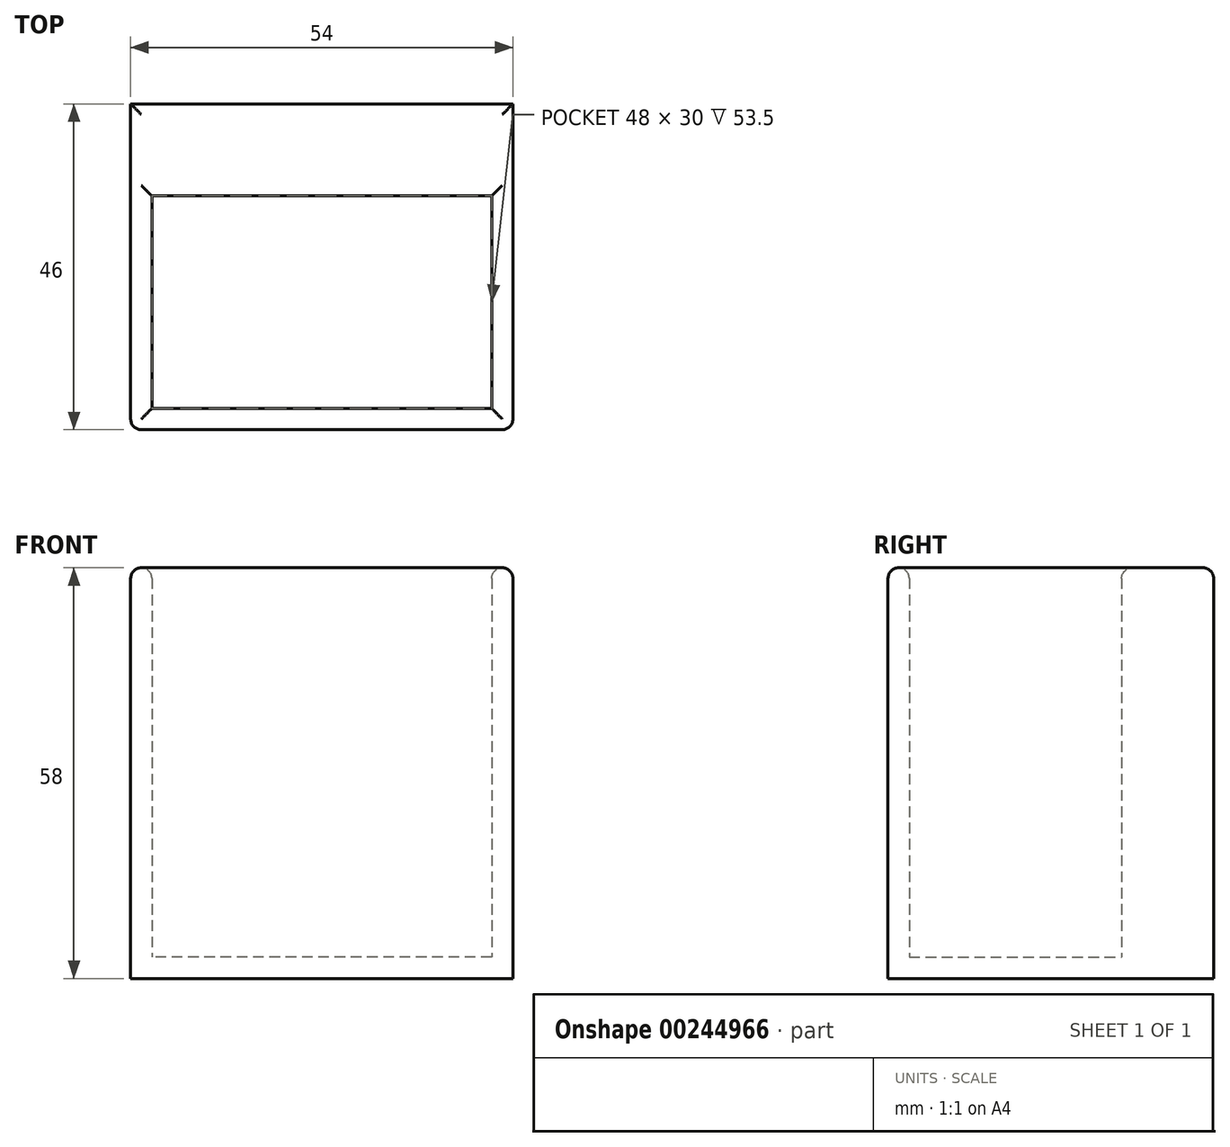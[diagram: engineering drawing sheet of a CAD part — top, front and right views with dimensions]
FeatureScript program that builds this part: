
annotation { "Feature Type Name" : "Feature", "Feature Type Description" : "" }
export const myFeature = defineFeature(function(context is Context, id is Id, definition is map)
    precondition{}
    {
        {
            var Q0;
            Q0=qCreatedBy(makeId("Top.planeOp"),FACE);
            var sketch = newSketch(context, id + "F0", { "sketchPlane" : qUnion([Q0])});
            skLineSegment(sketch, "E0.bottom", {"start": v(27, -18) * mm, "end": v(-27, -18) * mm});
            skLineSegment(sketch, "E0.top", {"start": v(27, 18) * mm, "end": v(-27, 18) * mm});
            skLineSegment(sketch, "E0.left", {"start": v(27, -18) * mm, "end": v(27, 18) * mm});
            skLineSegment(sketch, "E0.right", {"start": v(-27, -18) * mm, "end": v(-27, 18) * mm});
            skPoint(sketch, "E0.middle", {"position": v(0, 0) * mm});
            skSolve(sketch);
        }
        {
            var Q0;
            Q0 = qSketchRegion(id + "F0", true);
            extrude(context, id + "F1", {"entities" : qUnion([Q0]), "depth" : (55 + 3) * mm});
        }
        {
            var Q0;
            Q0=makeQuery(id+"F1.opExtrude","CAP_FACE",FACE,{"disambiguationData":[OSD([sQuery(id+"F0.wireOp",EDGE,"E0.bottom"),sQuery(id+"F0.wireOp",EDGE,"E0.top"),sQuery(id+"F0.wireOp",EDGE,"E0.left"),sQuery(id+"F0.wireOp",EDGE,"E0.right")])],"isStart":false});
            shell(context, id + "F2", {"entities" : qUnion([Q0]), "thickness" : 3 * mm});
        }
        {
            var Q0;
            Q0=makeQuery(id+"F1.opExtrude","SWEPT_FACE",FACE,{"disambiguationData":[OSD([sQuery(id+"F0.wireOp",EDGE,"E0.top")])]});
            var sketch = newSketch(context, id + "F3", { "sketchPlane" : qUnion([Q0])});
            skLineSegment(sketch, "E1.0.0", {"start": v(-27, 0) * mm, "end": v(27, 0) * mm});
            skLineSegment(sketch, "E1.0.1", {"start": v(27, 0) * mm, "end": v(27, 58) * mm});
            skLineSegment(sketch, "E1.0.2", {"start": v(27, 58) * mm, "end": v(-27, 58) * mm});
            skLineSegment(sketch, "E1.0.3", {"start": v(-27, 58) * mm, "end": v(-27, 0) * mm});
            skSolve(sketch);
        }
        {
            var Q0;
            Q0 = qSketchRegion(id + "F3", true);
            extrude(context, id + "F4", {"entities" : qUnion([Q0]), "operationType" : NewBodyOperationType.ADD, "depth" : 10 * mm});
        }
        {
            var Q0;
            Q0=makeQuery(id+"F1.opExtrude","CAP_FACE",FACE,{"disambiguationData":[OSD([sQuery(id+"F0.wireOp",EDGE,"E0.bottom"),sQuery(id+"F0.wireOp",EDGE,"E0.top"),sQuery(id+"F0.wireOp",EDGE,"E0.left"),sQuery(id+"F0.wireOp",EDGE,"E0.right")])],"isStart":false});
            var Q1;
            Q1=makeQuery(id+"F1.opExtrude","SWEPT_EDGE",EDGE,{"disambiguationData":[OSD([sQuery(id+"F0.wireOp",EDGE,"E0.bottom"),sQuery(id+"F0.wireOp",EDGE,"E0.right")])]});
            var Q2;
            Q2=makeQuery(id+"F1.opExtrude","SWEPT_EDGE",EDGE,{"disambiguationData":[OSD([sQuery(id+"F0.wireOp",EDGE,"E0.bottom"),sQuery(id+"F0.wireOp",EDGE,"E0.left")])]});
            var Q3;
            Q3=makeQuery(id+"F1.opExtrude","SWEPT_EDGE",EDGE,{"disambiguationData":[OSD([sQuery(id+"F0.wireOp",EDGE,"E0.top"),sQuery(id+"F0.wireOp",EDGE,"E0.left")])]});
            var Q4;
            Q4=makeQuery(id+"F1.opExtrude","SWEPT_EDGE",EDGE,{"disambiguationData":[OSD([sQuery(id+"F0.wireOp",EDGE,"E0.top"),sQuery(id+"F0.wireOp",EDGE,"E0.right")])]});
            fillet(context, id + "F5", {"entities" : qUnion([Q0, Q1, Q2, Q3, Q4]), "radius" : 1.5 * mm, "tangentPropagation" : true, "allowEdgeOverflow" : false});
        }
    });
